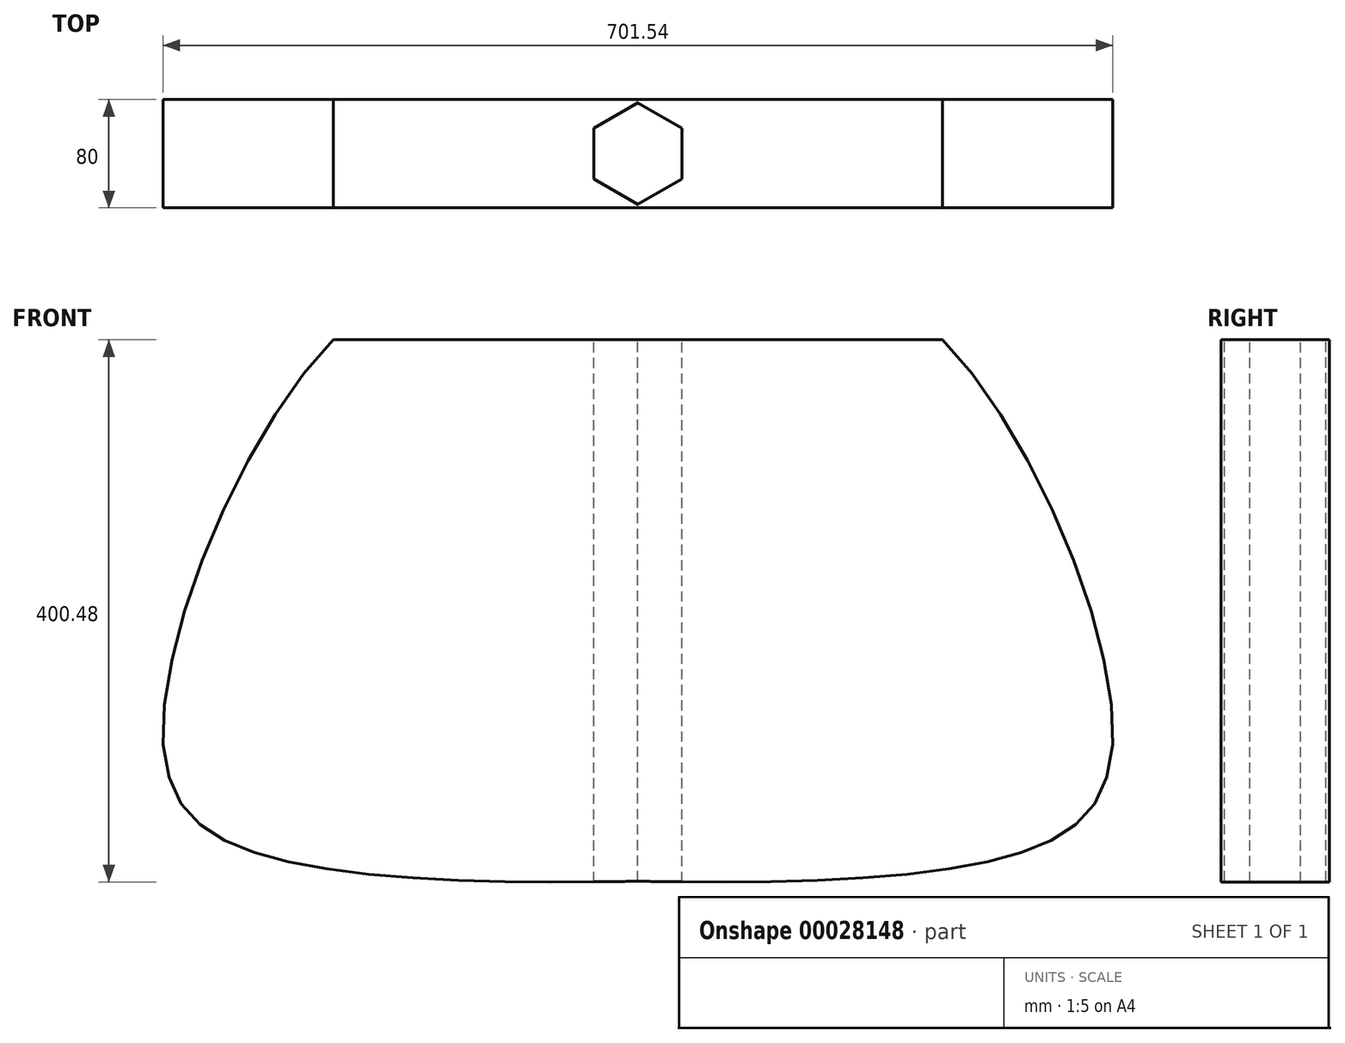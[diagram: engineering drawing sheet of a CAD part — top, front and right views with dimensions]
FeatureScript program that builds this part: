
annotation { "Feature Type Name" : "Feature", "Feature Type Description" : "" }
export const myFeature = defineFeature(function(context is Context, id is Id, definition is map)
    precondition{}
    {
        {
            var Q0;
            Q0=qCreatedBy(makeId("Front.planeOp"),FACE);
            var sketch = newSketch(context, id + "F0", { "sketchPlane" : qUnion([Q0])});
            skFitSpline(sketch, "E0", {"points": [v(-225, 198.7) * mm, v(-350, -106.53) * mm, v(-266.32, -184.9) * mm, v(0, -201.3) * mm], "startDerivative": vector(-503.13, -511.37) * mm, "endDerivative": vector(701.84, 9.75) * mm});
            skLineSegment(sketch, "E1", {"start": v(0, -264.48) * mm, "end": v(0, 165.15) * mm, "construction": true});
            skFitSpline(sketch, "E2.MirrorCS", {"points": [v(225, 198.7) * mm, v(350, -106.53) * mm, v(266.32, -184.9) * mm, v(0, -201.3) * mm], "startDerivative": vector(503.13, -511.37) * mm, "endDerivative": vector(-701.84, 9.75) * mm});
            skLineSegment(sketch, "E3", {"start": v(-225, 198.7) * mm, "end": v(225, 198.7) * mm});
            skSolve(sketch);
        }
        {
            var Q0;
            Q0=makeQuery(id+"F0.imprint","IMPRINT",FACE,{"disambiguationData":[TD([[makeQuery(id+"F0.imprint","IMPRINT",EDGE,{"derivedFrom":sQuery(id+"F0.wireOp",EDGE,"E0")}),1.0]])]});
            var Q1;
            Q1 = qSketchRegion(id + "F2", true);
            var Q2;
            Q2=sQuery(id+"F0.wireOp",EDGE,"E0");
            var Q3;
            Q3=sQuery(id+"F0.wireOp",EDGE,"E2.MirrorCS");
            var Q4;
            Q4=sQuery(id+"F0.wireOp",EDGE,"E3");
            extrude(context, id + "F1", {"entities" : qUnion([Q0, Q1]), "surfaceEntities" : qUnion([Q2, Q3, Q4]), "depth" : 80 * mm});
        }
        {
            var Q0;
            Q0=makeQuery(id+"F1.opExtrude","SWEPT_FACE",FACE,{"disambiguationData":[OSD([sQuery(id+"F0.wireOp",EDGE,"E3")])]});
            var sketch = newSketch(context, id + "F2", { "sketchPlane" : qUnion([Q0])});
            skCircle(sketch, "E4.cCircle", {"center": v(0, -40) * mm, "radius": 32.48 * mm, "construction": true});
            skLineSegment(sketch, "E4.0", {"start": v(0, -2.5) * mm, "end": v(32.48, -21.25) * mm});
            skLineSegment(sketch, "E4.1", {"start": v(32.48, -21.25) * mm, "end": v(32.48, -58.75) * mm});
            skLineSegment(sketch, "E4.2", {"start": v(32.48, -58.75) * mm, "end": v(0, -77.5) * mm});
            skLineSegment(sketch, "E4.3", {"start": v(0, -77.5) * mm, "end": v(-32.48, -58.75) * mm});
            skLineSegment(sketch, "E4.4", {"start": v(-32.48, -58.75) * mm, "end": v(-32.48, -21.25) * mm});
            skLineSegment(sketch, "E4.5", {"start": v(-32.48, -21.25) * mm, "end": v(0, -2.5) * mm});
            skPoint(sketch, "E4.0.midPoint", {"position": v(16.24, -11.87) * mm});
            skSolve(sketch);
        }
        {
            var Q0;
            Q0=makeQuery(id+"F2.imprint","IMPRINT",FACE,{"disambiguationData":[TD([[makeQuery(id+"F2.imprint","IMPRINT",EDGE,{"derivedFrom":sQuery(id+"F2.wireOp",EDGE,"E4.0")}),-1.0]])]});
            extrude(context, id + "F3", {"entities" : qUnion([Q0]), "operationType" : NewBodyOperationType.REMOVE, "oppositeDirection" : true, "depth" : 433.4 * mm});
        }
    });
